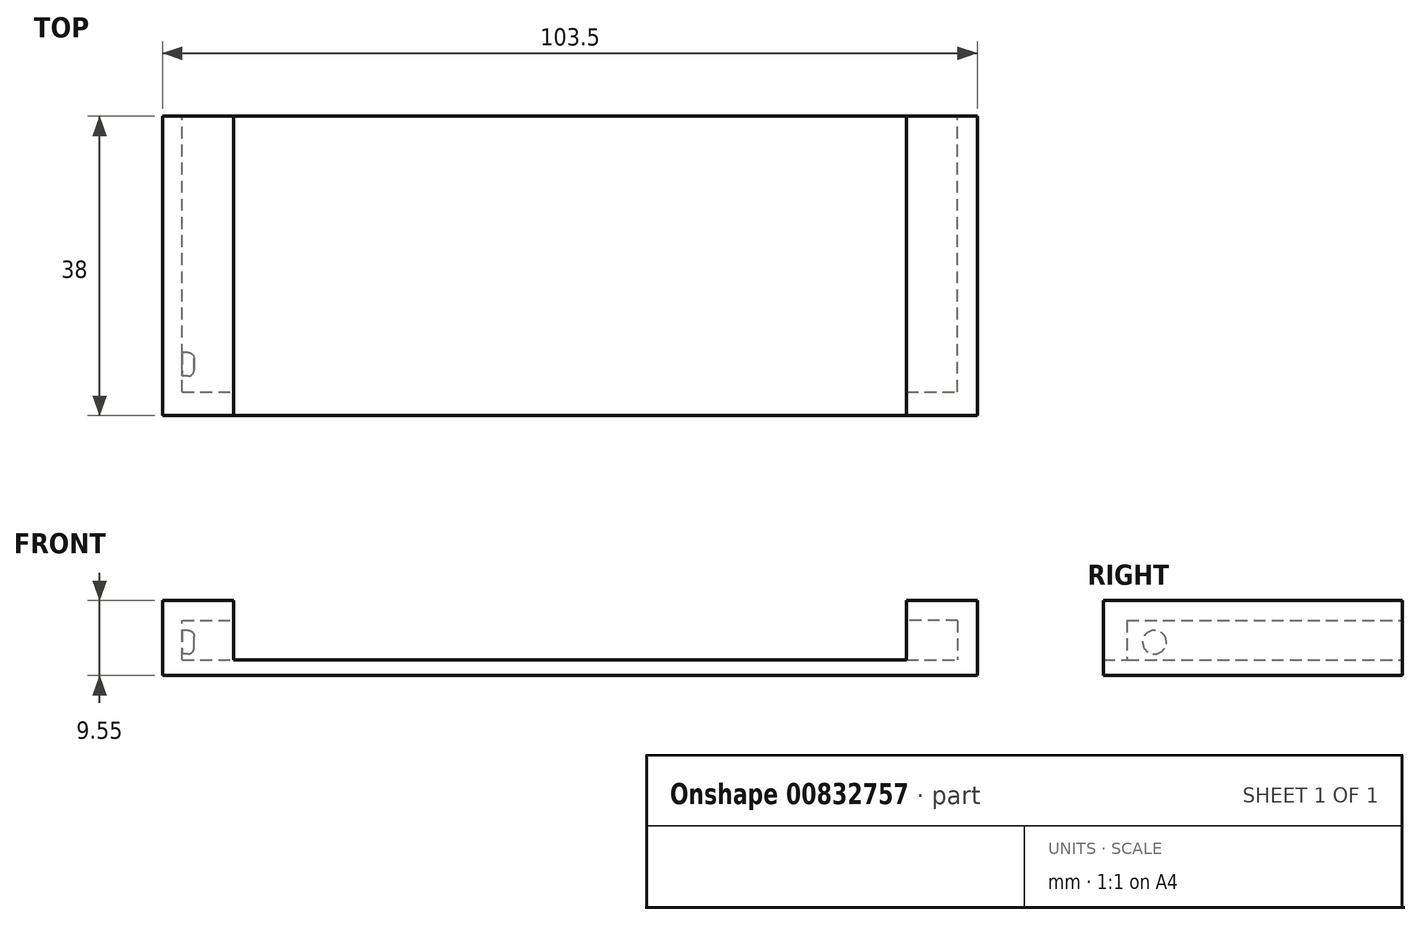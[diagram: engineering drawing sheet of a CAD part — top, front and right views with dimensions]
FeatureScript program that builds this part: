
annotation { "Feature Type Name" : "Feature", "Feature Type Description" : "" }
export const myFeature = defineFeature(function(context is Context, id is Id, definition is map)
    precondition{}
    {
        {
            var Q0;
            Q0=qCreatedBy(makeId("Top.planeOp"),FACE);
            var sketch = newSketch(context, id + "F0", { "sketchPlane" : qUnion([Q0])});
            skLineSegment(sketch, "E0.bottom", {"start": v(0, 0) * mm, "end": v(98.5, 0) * mm});
            skLineSegment(sketch, "E0.top", {"start": v(0, 38) * mm, "end": v(98.5, 38) * mm});
            skLineSegment(sketch, "E0.left", {"start": v(0, 0) * mm, "end": v(0, 38) * mm});
            skLineSegment(sketch, "E0.right", {"start": v(98.5, 0) * mm, "end": v(98.5, 38) * mm});
            skSolve(sketch);
        }
        {
            var Q0;
            Q0 = qSketchRegion(id + "F0", true);
            extrude(context, id + "F1", {"entities" : qUnion([Q0]), "depth" : 2 * mm, "offsetDistance" : 25 * mm});
        }
        {
            var Q0;
            Q0=makeQuery(id+"F1.opExtrude","SWEPT_FACE",FACE,{"disambiguationData":[OSD([sQuery(id+"F0.wireOp",EDGE,"E0.top")])]});
            var sketch = newSketch(context, id + "F2", { "sketchPlane" : qUnion([Q0])});
            skLineSegment(sketch, "E1.bottom", {"start": v(-98.5, 0) * mm, "end": v(-101, 0) * mm});
            skLineSegment(sketch, "E1.right", {"start": v(-101, 0) * mm, "end": v(-101, 9.55) * mm});
            skLineSegment(sketch, "E2.top", {"start": v(-98.5, 7) * mm, "end": v(-92, 7) * mm});
            skLineSegment(sketch, "E2.right", {"start": v(-92, 9.55) * mm, "end": v(-92, 7) * mm});
            skLineSegment(sketch, "E3", {"start": v(-98.5, 7) * mm, "end": v(-98.5, 0) * mm});
            skLineSegment(sketch, "E4", {"start": v(-92, 9.55) * mm, "end": v(-101, 9.55) * mm});
            skLineSegment(sketch, "E5", {"start": v(0, 0) * mm, "end": v(0, 7) * mm});
            skLineSegment(sketch, "E6", {"start": v(0, 7) * mm, "end": v(-6.5, 7) * mm});
            skLineSegment(sketch, "E7", {"start": v(-6.5, 7) * mm, "end": v(-6.5, 9.55) * mm});
            skLineSegment(sketch, "E8", {"start": v(-6.5, 9.55) * mm, "end": v(2.5, 9.55) * mm});
            skLineSegment(sketch, "E9", {"start": v(2.5, 9.55) * mm, "end": v(2.5, 0) * mm});
            skLineSegment(sketch, "E10", {"start": v(2.5, 0) * mm, "end": v(0, 0) * mm});
            skSolve(sketch);
        }
        {
            var Q0;
            Q0 = qSketchRegion(id + "F2", true);
            extrude(context, id + "F3", {"entities" : qUnion([Q0]), "operationType" : NewBodyOperationType.ADD, "oppositeDirection" : true, "depth" : 35 * mm, "offsetDistance" : 25 * mm});
        }
        {
            var Q0;
            Q0=makeQuery(id+"F3.opExtrude","CAP_FACE",FACE,{"disambiguationData":[OSD([sQuery(id+"F2.wireOp",EDGE,"E5"),sQuery(id+"F2.wireOp",EDGE,"E6"),sQuery(id+"F2.wireOp",EDGE,"E7"),sQuery(id+"F2.wireOp",EDGE,"E8"),sQuery(id+"F2.wireOp",EDGE,"E9"),sQuery(id+"F2.wireOp",EDGE,"E10")])],"isStart":false});
            var sketch = newSketch(context, id + "F4", { "sketchPlane" : qUnion([Q0])});
            skLineSegment(sketch, "E11.bottom", {"start": v(-2.5, 9.55) * mm, "end": v(6.5, 9.55) * mm});
            skLineSegment(sketch, "E11.top", {"start": v(-2.5, 0) * mm, "end": v(6.5, 0) * mm});
            skLineSegment(sketch, "E11.left", {"start": v(-2.5, 9.55) * mm, "end": v(-2.5, 0) * mm});
            skLineSegment(sketch, "E11.right", {"start": v(6.5, 9.55) * mm, "end": v(6.5, 0) * mm});
            skLineSegment(sketch, "E12.bottom", {"start": v(101, 9.55) * mm, "end": v(92, 9.55) * mm});
            skLineSegment(sketch, "E12.top", {"start": v(101, 0) * mm, "end": v(92, 0) * mm});
            skLineSegment(sketch, "E12.left", {"start": v(101, 9.55) * mm, "end": v(101, 0) * mm});
            skLineSegment(sketch, "E12.right", {"start": v(92, 9.55) * mm, "end": v(92, 0) * mm});
            skSolve(sketch);
        }
        {
            var Q0;
            Q0 = qSketchRegion(id + "F4", true);
            extrude(context, id + "F5", {"entities" : qUnion([Q0]), "operationType" : NewBodyOperationType.ADD, "depth" : 3 * mm, "offsetDistance" : 25 * mm});
        }
        {
            var Q0;
            Q0=makeQuery(id+"F3.opExtrude","SWEPT_FACE",FACE,{"disambiguationData":[OSD([sQuery(id+"F2.wireOp",EDGE,"E5")])]});
            var sketch = newSketch(context, id + "F6", { "sketchPlane" : qUnion([Q0])});
            skCircle(sketch, "E13", {"center": v(6.5, 4.25) * mm, "radius": 1.5 * mm});
            skSolve(sketch);
        }
        {
            var Q0;
            Q0 = qSketchRegion(id + "F6", true);
            extrude(context, id + "F7", {"entities" : qUnion([Q0]), "operationType" : NewBodyOperationType.ADD, "depth" : 1.5 * mm, "offsetDistance" : 25 * mm});
        }
        {
            var Q0;
            Q0=makeQuery(id+"F7.opExtrude","CAP_EDGE",EDGE,{"disambiguationData":[OSD([sQuery(id+"F6.wireOp",EDGE,"E13")])],"isStart":false});
            var Q1;
            Q1=makeQuery(id+"F7.opExtrude","CAP_EDGE",EDGE,{"disambiguationData":[OSD([sQuery(id+"F6.wireOp",EDGE,"E13")])],"isStart":true});
            fillet(context, id + "F8", {"entities" : qUnion([Q0, Q1]), "radius" : .75 * mm, "tangentPropagation" : true, "allowEdgeOverflow" : false});
        }
    });
